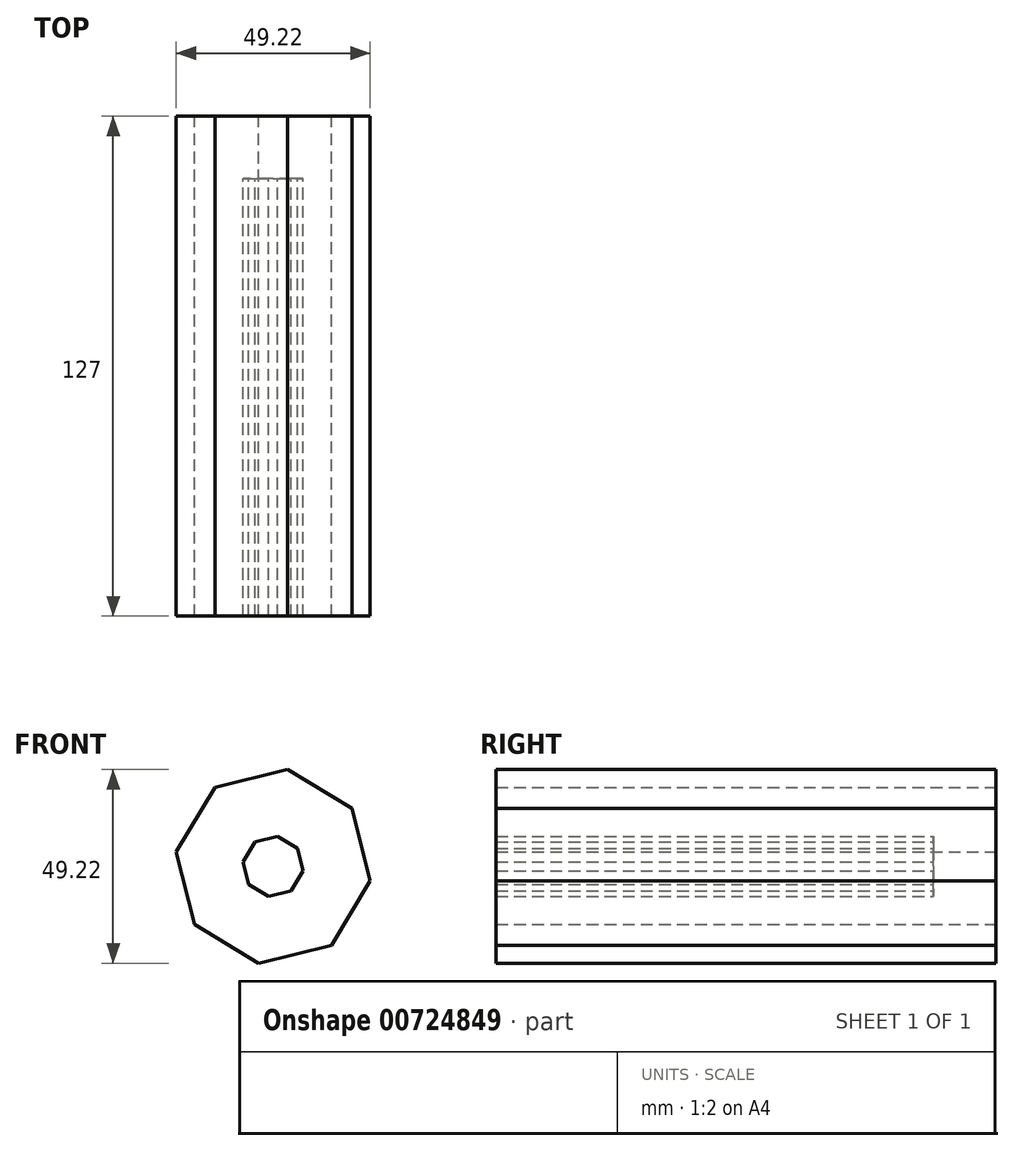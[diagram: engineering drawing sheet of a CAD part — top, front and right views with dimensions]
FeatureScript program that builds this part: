
annotation { "Feature Type Name" : "Feature", "Feature Type Description" : "" }
export const myFeature = defineFeature(function(context is Context, id is Id, definition is map)
    precondition{}
    {
        {
            var Q0;
            Q0=qCreatedBy(makeId("Front.planeOp"),FACE);
            var sketch = newSketch(context, id + "F0", { "sketchPlane" : qUnion([Q0])});
            skCircle(sketch, "E0.cCircle", {"center": v(0, 0) * mm, "radius": 24.9 * mm, "construction": true});
            skLineSegment(sketch, "E0.0", {"start": v(20.03, 14.78) * mm, "end": v(24.61, -3.71) * mm});
            skLineSegment(sketch, "E0.1", {"start": v(24.61, -3.71) * mm, "end": v(14.78, -20.03) * mm});
            skLineSegment(sketch, "E0.2", {"start": v(14.78, -20.03) * mm, "end": v(-3.71, -24.61) * mm});
            skLineSegment(sketch, "E0.3", {"start": v(-3.71, -24.61) * mm, "end": v(-20.03, -14.78) * mm});
            skLineSegment(sketch, "E0.4", {"start": v(-20.03, -14.78) * mm, "end": v(-24.61, 3.71) * mm});
            skLineSegment(sketch, "E0.5", {"start": v(-24.61, 3.71) * mm, "end": v(-14.78, 20.03) * mm});
            skLineSegment(sketch, "E0.6", {"start": v(-14.78, 20.03) * mm, "end": v(3.71, 24.61) * mm});
            skLineSegment(sketch, "E0.7", {"start": v(3.71, 24.61) * mm, "end": v(20.03, 14.78) * mm});
            skSolve(sketch);
        }
        {
            var Q0;
            Q0=makeQuery(id+"F0.imprint","IMPRINT",FACE,{"disambiguationData":[TD([[makeQuery(id+"F0.imprint","IMPRINT",EDGE,{"derivedFrom":sQuery(id+"F0.wireOp",EDGE,"E0.0")}),-1.0]])]});
            extrude(context, id + "F1", {"entities" : qUnion([Q0]), "depth" : 127 * mm, "offsetDistance" : 25.4 * mm});
        }
        {
            var Q0;
            Q0=makeQuery(id+"F1.opExtrude","CAP_FACE",FACE,{"disambiguationData":[OSD([sQuery(id+"F0.wireOp",EDGE,"E0.0"),sQuery(id+"F0.wireOp",EDGE,"E0.1"),sQuery(id+"F0.wireOp",EDGE,"E0.2"),sQuery(id+"F0.wireOp",EDGE,"E0.3"),sQuery(id+"F0.wireOp",EDGE,"E0.4"),sQuery(id+"F0.wireOp",EDGE,"E0.5"),sQuery(id+"F0.wireOp",EDGE,"E0.6"),sQuery(id+"F0.wireOp",EDGE,"E0.7")])],"isStart":false});
            shell(context, id + "F2", {"entities" : qUnion([Q0]), "thickness" : 15.88 * mm});
        }
    });
